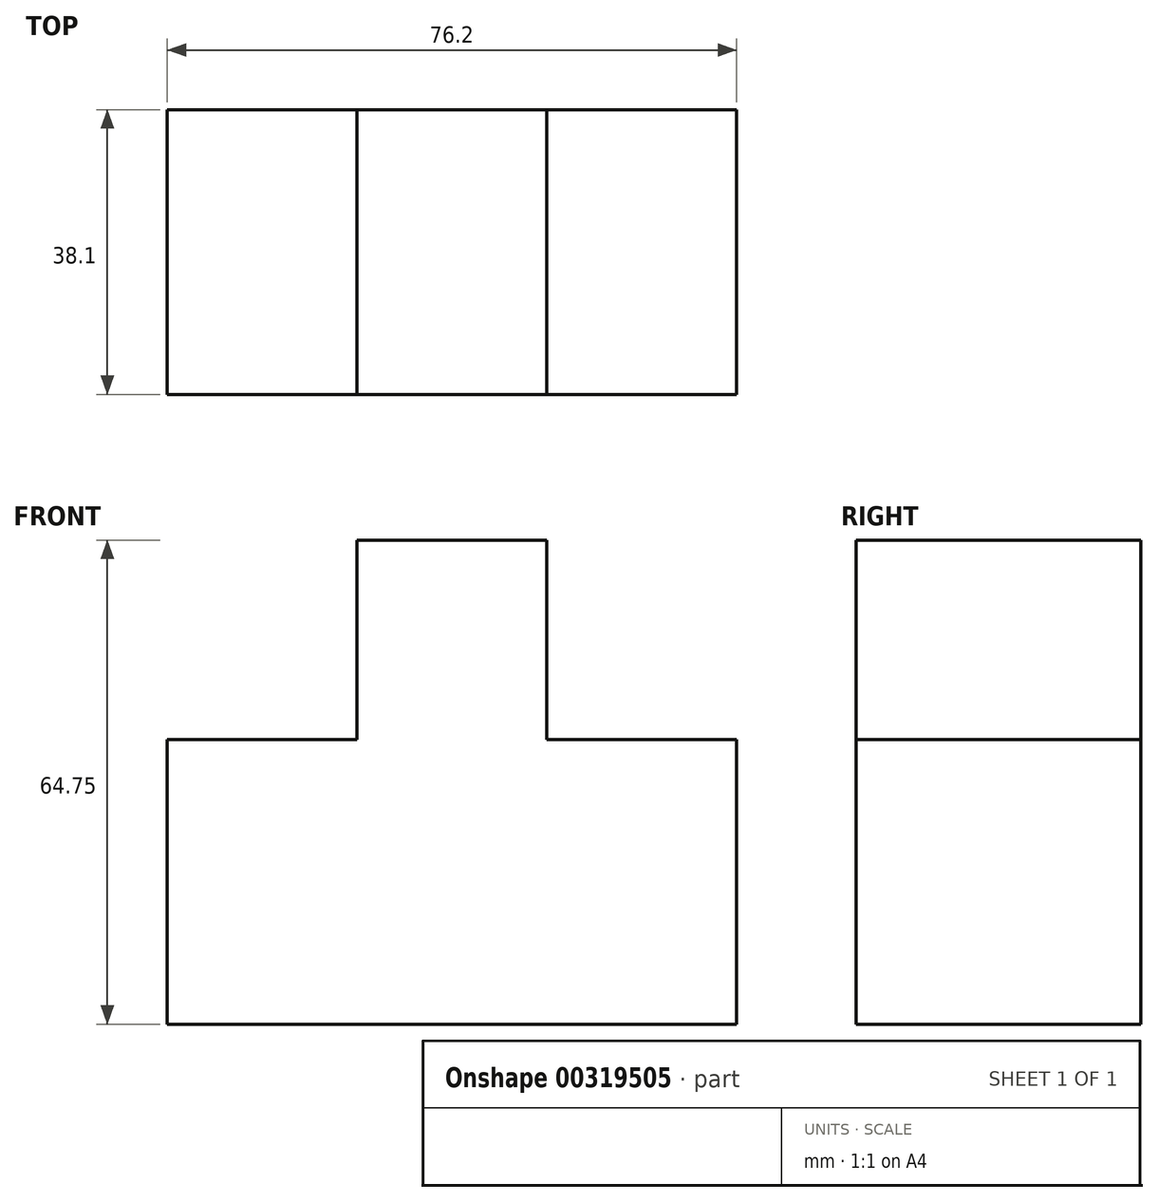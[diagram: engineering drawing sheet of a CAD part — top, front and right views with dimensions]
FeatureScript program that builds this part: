
annotation { "Feature Type Name" : "Feature", "Feature Type Description" : "" }
export const myFeature = defineFeature(function(context is Context, id is Id, definition is map)
    precondition{}
    {
        {
            var Q0;
            Q0=qCreatedBy(makeId("Front.planeOp"),FACE);
            var sketch = newSketch(context, id + "F0", { "sketchPlane" : qUnion([Q0])});
            skLineSegment(sketch, "E0", {"start": v(-47.2, -34.94) * mm, "end": v(29, -34.94) * mm});
            skLineSegment(sketch, "E1", {"start": v(29, -34.94) * mm, "end": v(29, 3.16) * mm});
            skLineSegment(sketch, "E2", {"start": v(29, 3.16) * mm, "end": v(3.6, 3.16) * mm});
            skLineSegment(sketch, "E3", {"start": v(3.6, 3.16) * mm, "end": v(3.6, 29.8) * mm});
            skLineSegment(sketch, "E4", {"start": v(3.6, 29.8) * mm, "end": v(-21.8, 29.8) * mm});
            skLineSegment(sketch, "E5", {"start": v(-21.8, 29.8) * mm, "end": v(-21.8, 3.16) * mm});
            skLineSegment(sketch, "E6", {"start": v(-21.8, 3.16) * mm, "end": v(-47.2, 3.16) * mm});
            skLineSegment(sketch, "E7", {"start": v(-47.2, 3.16) * mm, "end": v(-47.2, -34.94) * mm});
            skSolve(sketch);
        }
        {
            var Q0;
            Q0=makeQuery(id+"F0.imprint","IMPRINT",FACE,{"disambiguationData":[TD([[makeQuery(id+"F0.imprint","IMPRINT",EDGE,{"derivedFrom":sQuery(id+"F0.wireOp",EDGE,"E0")}),1.0]])]});
            extrude(context, id + "F1", {"entities" : qUnion([Q0]), "depth" : 38.1 * mm});
        }
    });
